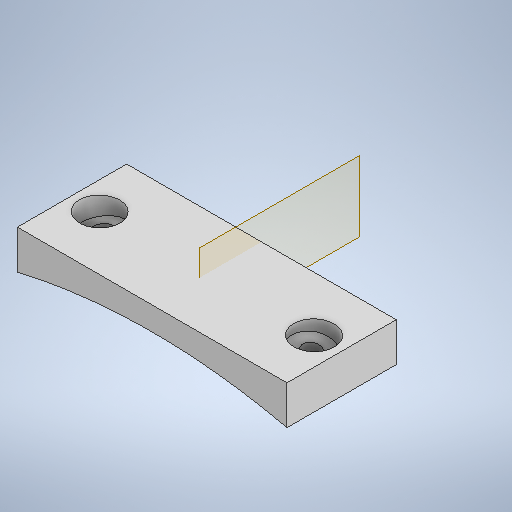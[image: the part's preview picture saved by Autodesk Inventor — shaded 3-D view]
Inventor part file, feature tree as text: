
AUTODESK INVENTOR PART (.ipt)
format: ipt  version: 2025 (Build 290162000, 162)  size: 327,680 bytes
history: native  units: in
note: dims shown in document units (in); Inventor stores cm internally (conversion verified against a paired STEP export)
features: sketch x7, extrude x6, mirror x2, revolve x1, plane x1
ambient origin geometry x8: Origin, YZ Plane, XZ Plane, XY Plane, X Axis, Y Axis, Z Axis, Center Point
bodies: Solid1 (feature_tree)
feature tree (17):
  extrude  "Extrusion1"  Depth=1.0in
  extrude  "Extrusion2"  Depth=2.0in TaperAngle=0.0deg
  revolve  "Revolution1"  [1 undecoded]
  plane  "Work Plane2"
  mirror  "Mirror1"
  extrude  "Extrusion3"  Depth=0.1175in
  extrude  "Extrusion4"  TaperAngle=90.0deg  [1 undecoded]
  extrude  "Extrusion5"  TaperAngle=90.0deg  [1 undecoded]
  extrude  "Extrusion6"  Depth=1.0in
  mirror  "Mirror5"
  sketch  "Sketch3"  dims[d11=4.0in d12=1.0in]
  sketch  "Sketch4"  dims[d13=2.0in d14=0.0in d20=2.0in d21=0.0in]
  sketch  "Sketch6"  dims[d39=0.12in d40=1.395in]
  sketch  "Sketch7"  dims[d41=0.1175in d42=0.0675in]
  sketch  "Sketch8"  dims[d43=0.25in d44=90.0deg]
  sketch  "Sketch9"  dims[d45=0.1575in d46=90.0deg]
  sketch  "Sketch10"  dims[d47=0.15in d48=1.0in d49=0.686in d50=90.0deg d51=-2.0in d52=0.15in d53=0.55in d54=90.0deg d55=2.0in d56=0.0in d57=0.1in d58=2.0in d59=0.0in d60=1.25in d61=0.0in d62=0.75in d63=0.0in]
note: 3 required parameter values undecoded (feature->parameter linkage not recoverable at this tier; creation-order binding heuristic only, values carry confidence <= 0.55)